# Revit family: LHV6
name_source: partatom
category: Lighting Fixtures
revit_build: Autodesk Revit Architecture 2012 (Build: 20110309_2315(x64)
units: mm (PartAtom-declared; Revit-internal decimal feet)

## types (1)
- LHA6
    Apparent Load = 0 VA
    Backbox = White
    Color Filter = 16777215
    Default Elevation = 48.000"
    Description = VersaBay® luminaires are the new industry standard for fluorescent high bay lighting with Advanced Thermal Management, serviceability, and performance that is unrivaled in the marketplace.
    Dimming Lamp Color Temperature Shift = <None>
    Emit from Line Length = 30.000"
    Glass = Glass
    Lamp = F32T8
    Light Source Symbol Size = 2.000"
    Manufacturer = Columbia Lighting
    Manufacturer Fax = 866-898-1065
    Model = LHA6
    Product Documentation Link = http://www.columbialighting.com
    Product Page URL = http://www.columbialighting.com
    URL = http://www.columbialighting.com
    Wattage Comments = 222 W

## geometry (parser evidence)
native form markers: Sweep x1
no freeform markers — native parametric forms only
